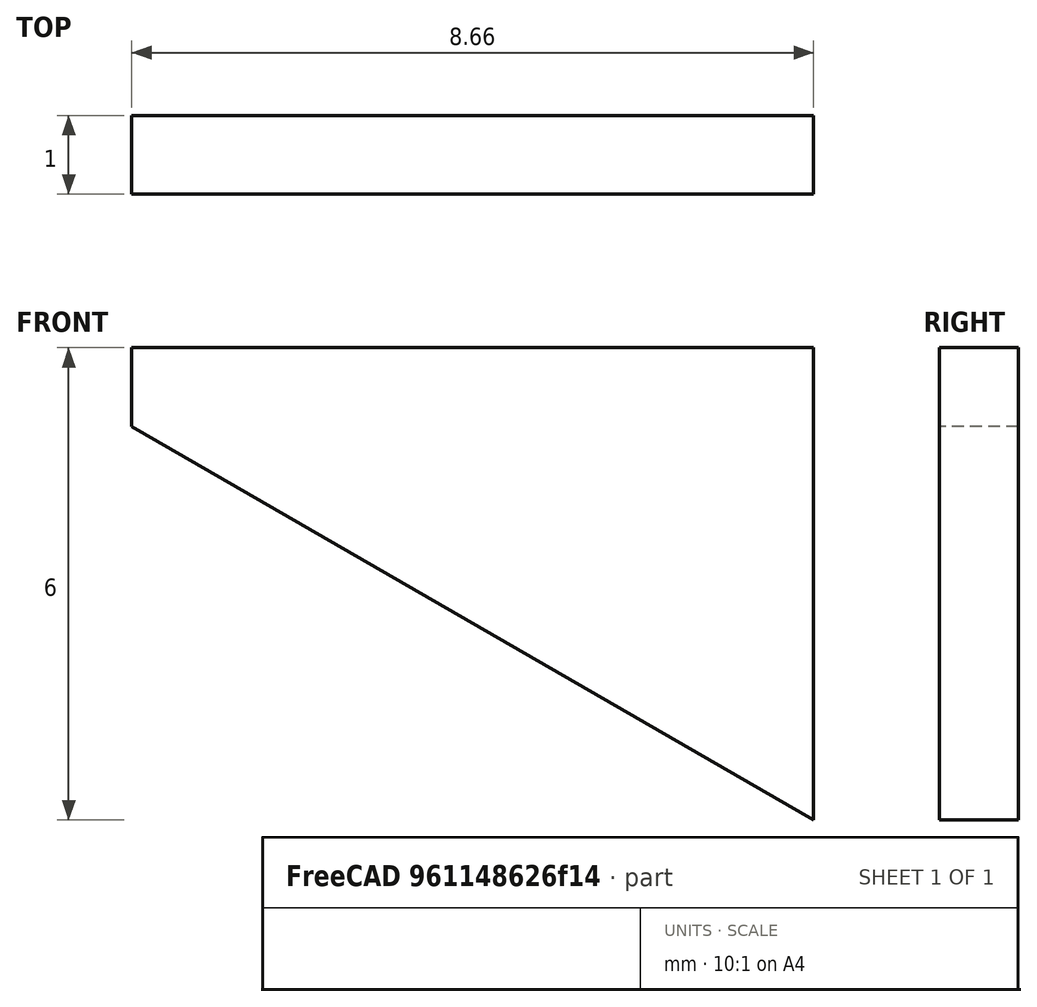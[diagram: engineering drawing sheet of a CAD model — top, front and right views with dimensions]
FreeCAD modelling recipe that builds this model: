
FCSTD DOCUMENT  (FreeCAD 1.0R39109 (Git))
Label: 30
License: All rights reserved
LicenseURL: http://en.wikipedia.org/wiki/All_rights_reserved
objects: PartDesign::SubShapeBinder×5, Mesh::Feature×5, Sketcher::SketchObject×1, PartDesign::Pad×1, PartDesign::Body×1
note: 11 computed .brp shape members not serialized (recipe doc carries the construction recipe); baked Part::Feature solids carry a one-line shape summary decoded from their .brp

FEATURE [Sketcher::SketchObject] Sketch
  ArcFitTolerance = 1e-06
  AttachmentSupport = -> [XZ_Plane]
  FullyConstrained = true
  MakeInternals = false
  MapMode = 5
  Placement = pos=(0,0,0) rot=(1,0,0;1.5708rad)
  sketch-geometry (4):
    g0: LineSegment StartX=0 StartY=0 StartZ=0 EndX=8.66025 EndY=0 EndZ=0
    g1: LineSegment StartX=8.66025 StartY=0 StartZ=0 EndX=8.66025 EndY=-6 EndZ=0
    g2: LineSegment StartX=8.66025 StartY=-6 StartZ=0 EndX=0 EndY=-1 EndZ=0
    g3: LineSegment StartX=0 StartY=-1 StartZ=0 EndX=0 EndY=0 EndZ=0
  constraints (11):
    c: Coincident(g-1,g0)
    c: PointOnObject(g0,g-1)
    c: Coincident(g0,g1)
    c: Vertical(g1)
    c: Coincident(g1,g2)
    c: PointOnObject(g2,g-2)
    c: Coincident(g2,g3)
    c: Coincident(g3,g0)
    c: Distance(g3,g3) = 1
    c: Distance(g2,g2) = 10
    c: Angle(g2,g0) = 0.523599
FEATURE [PartDesign::Pad] Pad
  Direction = (0,-1,2e-16)
  Length = 1
  Length2 = 10
  Placement = pos=(0,0,0) rot=(1,0,0;1.5708rad)
  Profile = -> Sketch
  ReferenceAxis = -> Sketch [N_Axis]
  Refine = true
  Suppressed = false
  Type = 0
FEATURE [PartDesign::SubShapeBinder] Binder  label="inlet"
  BindCopyOnChange = 0
  BindMode = 0
  ClaimChildren = false
  Context = -> Body [Binder.]
  Fuse = false
  MakeFace = true
  OffsetFill = false
  OffsetIntersection = false
  OffsetJoinType = 0
  OffsetOpenResult = false
  PartialLoad = false
  Refine = true
  Relative = true
  Support = -> [Pad[Face4]]
  _Version = 2
FEATURE [PartDesign::SubShapeBinder] Binder001  label="outlet"
  BindCopyOnChange = 0
  BindMode = 0
  ClaimChildren = false
  Context = -> Body [Binder001.]
  Fuse = false
  MakeFace = true
  OffsetFill = false
  OffsetIntersection = false
  OffsetJoinType = 0
  OffsetOpenResult = false
  PartialLoad = false
  Refine = true
  Relative = true
  Support = -> [Pad[Face2]]
  _Version = 2
FEATURE [PartDesign::SubShapeBinder] Binder002  label="top"
  BindCopyOnChange = 0
  BindMode = 0
  ClaimChildren = false
  Context = -> Body [Binder002.]
  Fuse = false
  MakeFace = true
  OffsetFill = false
  OffsetIntersection = false
  OffsetJoinType = 0
  OffsetOpenResult = false
  PartialLoad = false
  Refine = true
  Relative = true
  Support = -> [Pad[Face1]]
  _Version = 2
FEATURE [PartDesign::SubShapeBinder] Binder003  label="bottom"
  BindCopyOnChange = 0
  BindMode = 0
  ClaimChildren = false
  Context = -> Body [Binder003.]
  Fuse = false
  MakeFace = true
  OffsetFill = false
  OffsetIntersection = false
  OffsetJoinType = 0
  OffsetOpenResult = false
  PartialLoad = false
  Refine = true
  Relative = true
  Support = -> [Pad[Face3]]
  _Version = 2
FEATURE [PartDesign::SubShapeBinder] Binder004  label="sides"
  BindCopyOnChange = 0
  BindMode = 0
  ClaimChildren = false
  Context = -> Body [Binder004.]
  Fuse = false
  MakeFace = true
  OffsetFill = false
  OffsetIntersection = false
  OffsetJoinType = 0
  OffsetOpenResult = false
  PartialLoad = false
  Refine = true
  Relative = true
  Support = -> [Pad[Face6,Face5]]
  _Version = 2
FEATURE [PartDesign::Body] Body
  AllowCompound = false
  Group = -> [Sketch,Pad,Binder,Binder001,Binder002,Binder003,Binder004]
  Origin = -> Origin
  Tip = -> Pad
FEATURE [Mesh::Feature] Mesh  label="inlet (Meshed)"
FEATURE [Mesh::Feature] Mesh001  label="outlet (Meshed)"
FEATURE [Mesh::Feature] Mesh002  label="top (Meshed)"
FEATURE [Mesh::Feature] Mesh003  label="bottom (Meshed)"
FEATURE [Mesh::Feature] Mesh004  label="sides (Meshed)"
